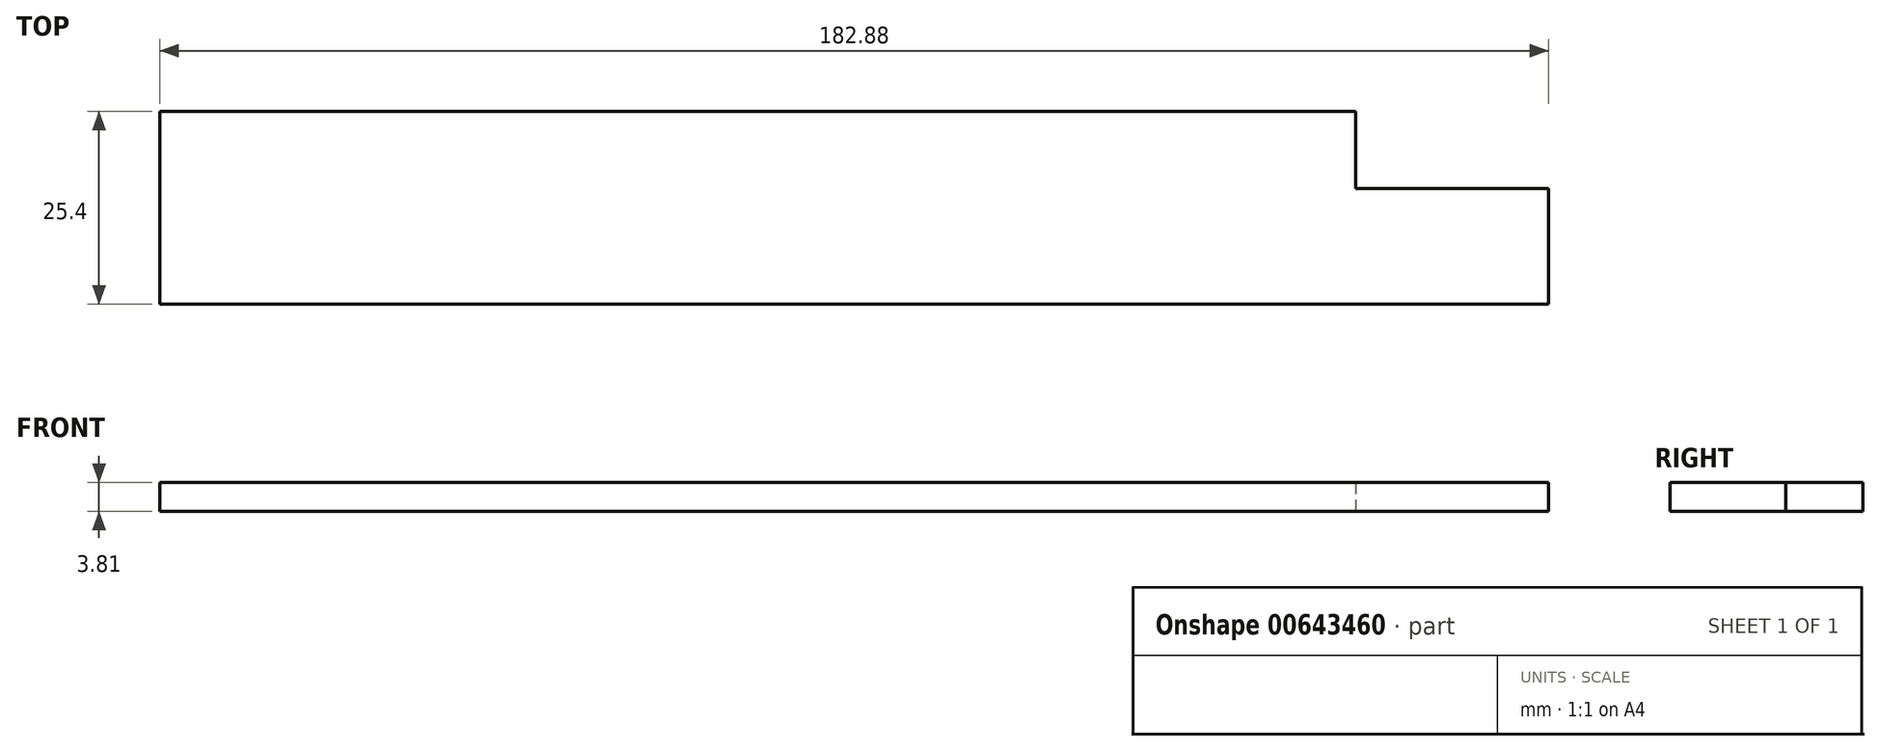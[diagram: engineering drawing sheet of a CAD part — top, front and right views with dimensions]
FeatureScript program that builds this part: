
annotation { "Feature Type Name" : "Feature", "Feature Type Description" : "" }
export const myFeature = defineFeature(function(context is Context, id is Id, definition is map)
    precondition{}
    {
        {
            var Q0;
            Q0=qCreatedBy(makeId("Top.planeOp"),FACE);
            var sketch = newSketch(context, id + "F0", { "sketchPlane" : qUnion([Q0])});
            skLineSegment(sketch, "E0.bottom", {"start": v(0, 0) * mm, "end": v(182.88, 0) * mm});
            skLineSegment(sketch, "E0.top", {"start": v(0, 25.4) * mm, "end": v(157.48, 25.4) * mm});
            skLineSegment(sketch, "E0.left", {"start": v(0, 0) * mm, "end": v(0, 25.4) * mm});
            skLineSegment(sketch, "E0.right", {"start": v(182.88, 0) * mm, "end": v(182.88, 15.24) * mm});
            skLineSegment(sketch, "E1", {"start": v(157.48, 25.4) * mm, "end": v(157.48, 15.24) * mm});
            skLineSegment(sketch, "E2", {"start": v(157.48, 15.24) * mm, "end": v(182.88, 15.24) * mm});
            skSolve(sketch);
        }
        {
            var Q0;
            Q0=makeQuery(id+"F0.imprint","IMPRINT",FACE,{"disambiguationData":[TD([[makeQuery(id+"F0.imprint","IMPRINT",EDGE,{"derivedFrom":sQuery(id+"F0.wireOp",EDGE,"E0.bottom")}),1.0]])]});
            extrude(context, id + "F1", {"entities" : qUnion([Q0]), "depth" : 3.8 * mm, "offsetDistance" : 25.4 * mm});
        }
    });
